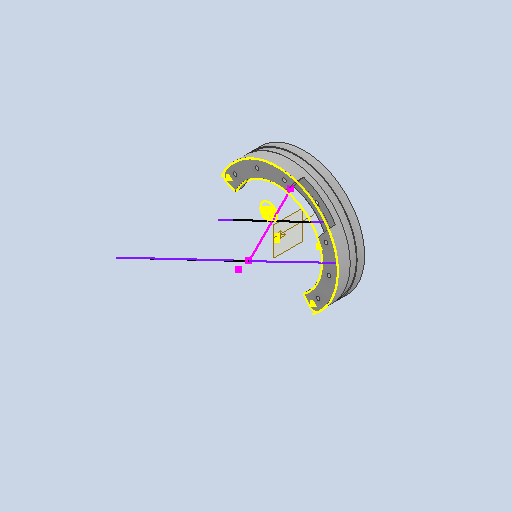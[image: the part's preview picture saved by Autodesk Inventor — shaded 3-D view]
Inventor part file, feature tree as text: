
AUTODESK INVENTOR PART (.ipt)
format: ipt  version: 2022 (Build 260153000, 153)  size: 299,008 bytes
history: native  units: in
note: dims shown in document units (in); Inventor stores cm internally (conversion verified against a paired STEP export)
features: other x10, reference x9, sketch x5, plane x3, extrude x2, projected_geometry x2, revolve x1, fillet x1, hole x1, pattern_circular x1
ambient origin geometry x8: Origin, YZ Plane, XZ Plane, XY Plane, X Axis, Y Axis, Z Axis, Center Point
bodies: Body1 (feature_tree)
feature tree (35):
  other  "Arbeitsachse1"
  plane  "Arbeitsebene4"
  revolve  "Umdrehung1"
  extrude  "Extrusion9"  Depth=0.1969in
  fillet  "Rundung2"  [1 undecoded]
  sketch  "Skizze13"  dims[d41=0.2362in]
  plane  "Arbeitsebene6"
  hole  "Bohrung1"  [1 undecoded]
  pattern_circular  "Runde Anordnung1"  Angle=360.0deg  [1 undecoded]
  sketch  "Skizze17"  dims[d43=0.0236in d44=360.0deg d46=0.3937in d47=0.0in d55=0.1969in d56=0.0118in d68=105.0deg d69=105.0deg d70=0.1102in d71=0.1102in d72=0.2362in d73=0.1969in d74=0.3937in d75=90.0deg d76=0.315in d77=0.8108in d78=4.7244in d79=360.0deg d81=0.1181in d82=0.3937in d83=0.0in]
  other  "Arbeitspunkt2"
  extrude  "Extrusion14"  Depth=0.3937in TaperAngle=0.0deg
  plane  "Arbeitsebene3"
  other  "Arbeitspunkt1"
  sketch  "Skizze10"  dims[d36=0.1575in d37=0.1969in d38=135.0deg]
  reference  "Referenz27"
  reference  "Referenz28"
  sketch  "Skizze11"  dims[d39=0.0118in d40=0.0984in]
  reference  "Referenz29"
  reference  "Referenz30"
  reference  "Referenz31"
  projected_geometry  "Projizierte Kontur8"
  projected_geometry  "Projizierte Kontur9"
  reference  "Referenz37"
  reference  "Referenz38"
  reference  "Referenz39"
  sketch  "Skizze16"  dims[d42=0.4724in]
  reference  "Referenz40"
  other  "Anglerfish_bonne_mamman_m12large_flipped_v0.iam"
  other  "00_Lid_Bonne_Mamman:1"
  other  "00_Coverglass:1"
  other  "Anglerfish_Lightplate_Tosslink:1"
  other  "Matchboxscope_M12_Lensadapter_v0:1"
  other  "00_toslink_launcher_v3:2"
  other  "00_toslink_launcher_v3:1"
note: 3 required parameter values undecoded (feature->parameter linkage not recoverable at this tier; creation-order binding heuristic only, values carry confidence <= 0.55)
